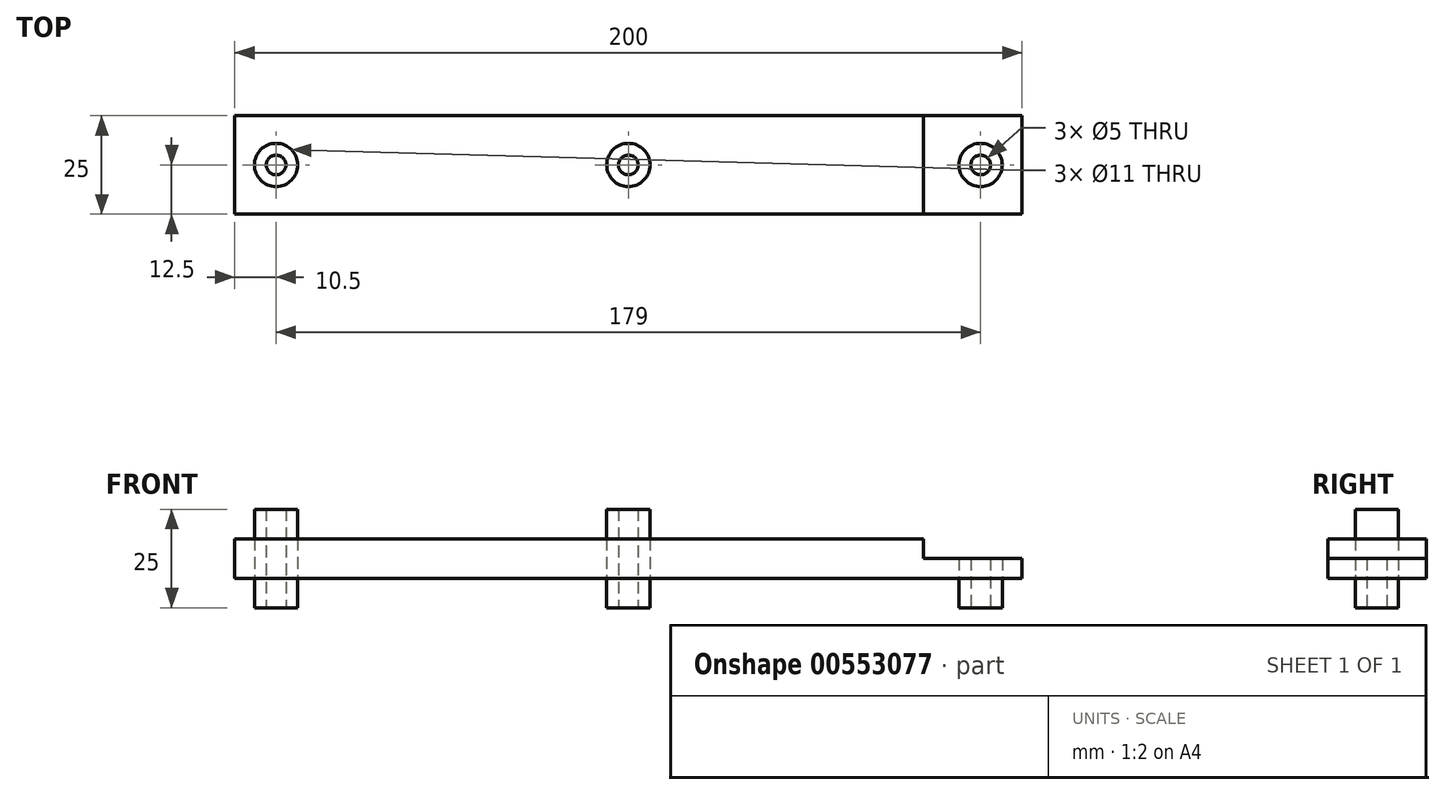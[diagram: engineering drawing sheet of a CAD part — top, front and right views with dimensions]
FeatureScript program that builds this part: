
annotation { "Feature Type Name" : "Feature", "Feature Type Description" : "" }
export const myFeature = defineFeature(function(context is Context, id is Id, definition is map)
    precondition{}
    {
        {
            var Q0;
            Q0=qCreatedBy(makeId("Top.planeOp"),FACE);
            var sketch = newSketch(context, id + "F0", { "sketchPlane" : qUnion([Q0])});
            skLineSegment(sketch, "E0.bottom", {"start": v(-100, -12.5) * mm, "end": v(100, -12.5) * mm});
            skLineSegment(sketch, "E0.top", {"start": v(-100, 12.5) * mm, "end": v(100, 12.5) * mm});
            skLineSegment(sketch, "E0.left", {"start": v(-100, -12.5) * mm, "end": v(-100, 12.5) * mm});
            skLineSegment(sketch, "E0.right", {"start": v(100, -12.5) * mm, "end": v(100, 12.5) * mm});
            skPoint(sketch, "E0.middle", {"position": v(0, 0) * mm});
            skCircle(sketch, "E1", {"center": v(-89.5, 0) * mm, "radius": 2.5 * mm});
            skCircle(sketch, "E2", {"center": v(-89.5, 0) * mm, "radius": 5.5 * mm});
            skLineSegment(sketch, "E3", {"start": v(-100, 0) * mm, "end": v(100, 0) * mm, "construction": true});
            skPoint(sketch, "E4", {"position": v(100, 0) * mm});
            skLineSegment(sketch, "E5", {"start": v(-95, 20.9) * mm, "end": v(-95, -21.64) * mm, "construction": true});
            skCircle(sketch, "E6", {"center": v(0, 0) * mm, "radius": 2.5 * mm});
            skCircle(sketch, "E7", {"center": v(0, 0) * mm, "radius": 5.5 * mm});
            skCircle(sketch, "E8", {"center": v(89.5, 0) * mm, "radius": 2.5 * mm});
            skCircle(sketch, "E9", {"center": v(89.5, 0) * mm, "radius": 5.5 * mm});
            skSolve(sketch);
        }
        {
            var Q0;
            Q0=makeQuery(id+"F0.imprint","IMPRINT",FACE,{"disambiguationData":[TD([[makeQuery(id+"F0.imprint","IMPRINT",EDGE,{"derivedFrom":sQuery(id+"F0.wireOp",EDGE,"E1")}),-1.0]])]});
            var Q1;
            Q1=makeQuery(id+"F0.imprint","IMPRINT",FACE,{"disambiguationData":[TD([[makeQuery(id+"F0.imprint","IMPRINT",EDGE,{"derivedFrom":sQuery(id+"F0.wireOp",EDGE,"E6")}),-1.0]])]});
            var Q2;
            Q2=makeQuery(id+"F0.imprint","IMPRINT",FACE,{"disambiguationData":[TD([[makeQuery(id+"F0.imprint","IMPRINT",EDGE,{"derivedFrom":sQuery(id+"F0.wireOp",EDGE,"E8")}),-1.0]])]});
            extrude(context, id + "F1", {"entities" : qUnion([Q0, Q1, Q2]), "endBound" : BoundingType.SYMMETRIC, "depth" : 25 * mm, "offsetDistance" : 25 * mm});
        }
        {
            var Q0;
            Q0=makeQuery(id+"F0.imprint","IMPRINT",FACE,{"disambiguationData":[TD([[makeQuery(id+"F0.imprint","IMPRINT",EDGE,{"derivedFrom":sQuery(id+"F0.wireOp",EDGE,"E0.bottom")}),1.0]])]});
            extrude(context, id + "F2", {"entities" : qUnion([Q0]), "endBound" : BoundingType.SYMMETRIC, "depth" : 10 * mm, "offsetDistance" : 25 * mm});
        }
        {
            var Q0;
            Q0=qCreatedBy(makeId("Front.planeOp"),FACE);
            var sketch = newSketch(context, id + "F3", { "sketchPlane" : qUnion([Q0])});
            skLineSegment(sketch, "E10", {"start": v(105, 20) * mm, "end": v(105, 0) * mm});
            skLineSegment(sketch, "E11", {"start": v(105, 0) * mm, "end": v(75, 0) * mm});
            skLineSegment(sketch, "E12", {"start": v(75, 0) * mm, "end": v(75, 20) * mm});
            skLineSegment(sketch, "E13", {"start": v(75, 20) * mm, "end": v(105, 20) * mm});
            skSolve(sketch);
        }
        {
            var Q0;
            Q0 = qSketchRegion(id + "F3", true);
            extrude(context, id + "F4", {"entities" : qUnion([Q0]), "operationType" : NewBodyOperationType.REMOVE, "endBound" : BoundingType.SYMMETRIC, "depth" : 30 * mm, "offsetDistance" : 25 * mm});
        }
    });
